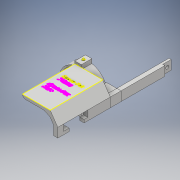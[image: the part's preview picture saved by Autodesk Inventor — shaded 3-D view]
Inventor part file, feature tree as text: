
AUTODESK INVENTOR PART (.ipt)
format: ipt  version: 2017 (Build 210142000, 142)  size: 653,312 bytes
history: native  units: mm
features: other x7, sketch x4, emboss x1
ambient origin geometry x8: Origin, YZ Plane, XZ Plane, XY Plane, X Axis, Y Axis, Z Axis, Center Point
bodies: Solid1 (feature_tree), Solid2 (feature_tree)
feature tree (12):
  other  "Y-axis-gimbal-part.ipt"
  sketch  "Sketch1"  dims[d0=22.424242mm]
  sketch  "Sketch2"  dims[d1=1.0mm d2=0.0mm]
  emboss  "Emboss1"
  sketch  "Sketch3"
  sketch  "Sketch4"
  other  "Solid1::Y-axis-gimbal-part.ipt"
  other  "Solid2::Y-axis-gimbal-part.ipt"
  other  "TaggingFeature1"
  other  "Work Point1"
  other  "Work Point2"
  other  "Work Point3"
